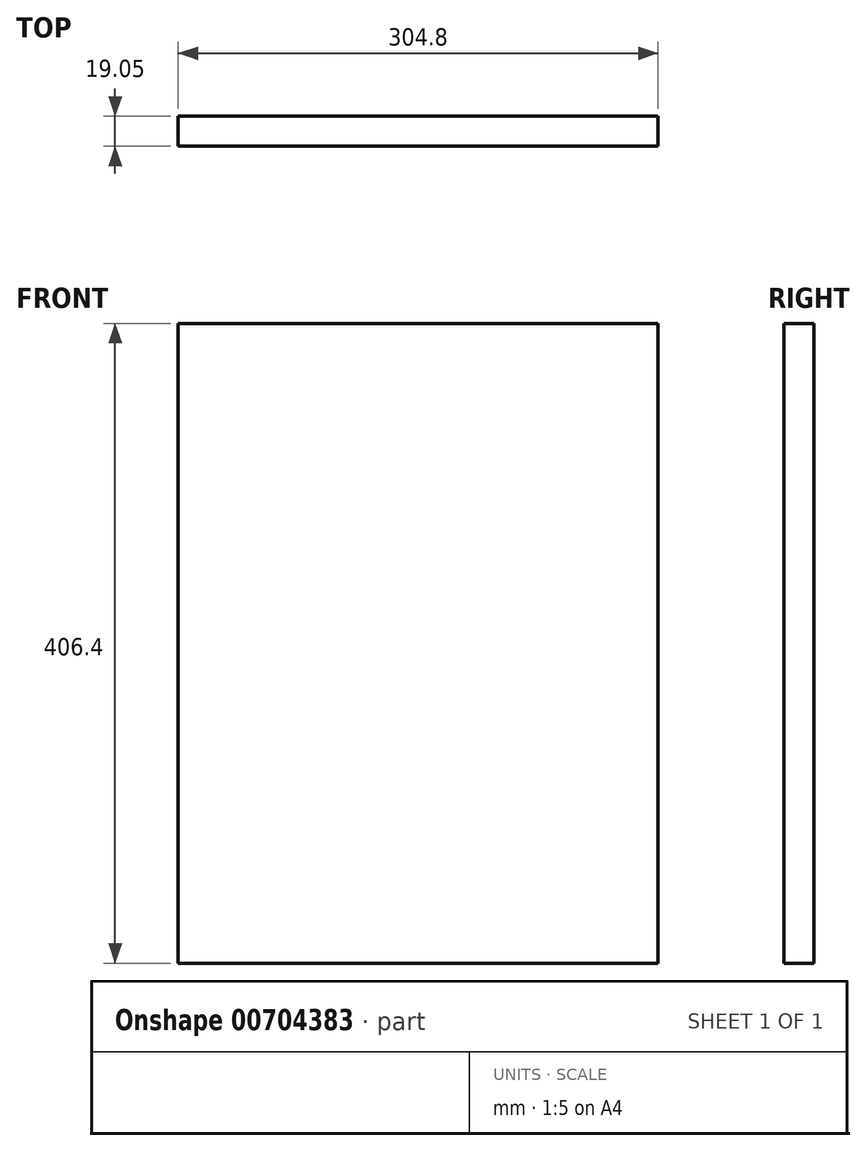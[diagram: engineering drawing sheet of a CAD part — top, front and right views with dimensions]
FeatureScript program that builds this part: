
annotation { "Feature Type Name" : "Feature", "Feature Type Description" : "" }
export const myFeature = defineFeature(function(context is Context, id is Id, definition is map)
    precondition{}
    {
        {
            var Q0;
            Q0=qCreatedBy(makeId("Front.planeOp"),FACE);
            var sketch = newSketch(context, id + "F0", { "sketchPlane" : qUnion([Q0])});
            skLineSegment(sketch, "E0.bottom", {"start": v(152.4, -203.2) * mm, "end": v(-152.4, -203.2) * mm});
            skLineSegment(sketch, "E0.top", {"start": v(152.4, 203.2) * mm, "end": v(-152.4, 203.2) * mm});
            skLineSegment(sketch, "E0.left", {"start": v(152.4, -203.2) * mm, "end": v(152.4, 203.2) * mm});
            skLineSegment(sketch, "E0.right", {"start": v(-152.4, -203.2) * mm, "end": v(-152.4, 203.2) * mm});
            skPoint(sketch, "E0.middle", {"position": v(0, 0) * mm});
            skSolve(sketch);
        }
        {
            var Q0;
            Q0 = qSketchRegion(id + "F0", true);
            extrude(context, id + "F1", {"entities" : qUnion([Q0]), "depth" : 19.05 * mm, "offsetDistance" : 25.4 * mm});
        }
    });
